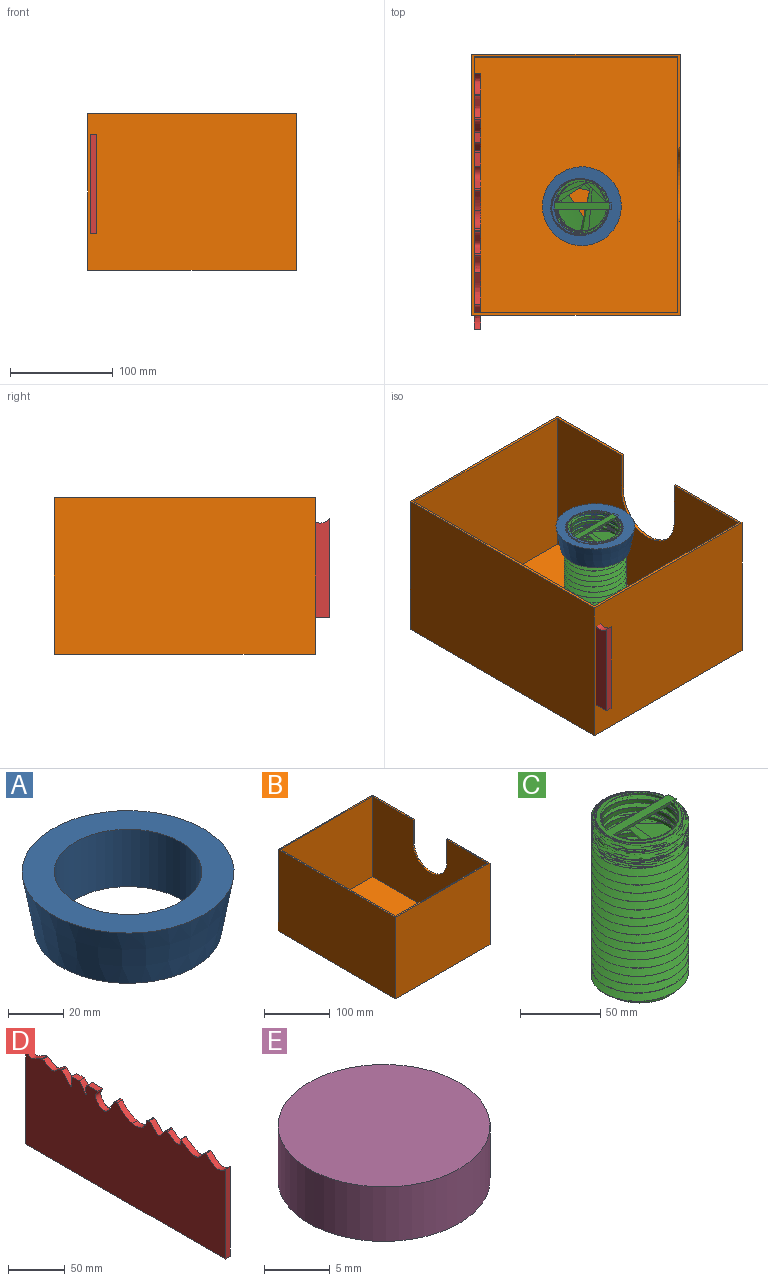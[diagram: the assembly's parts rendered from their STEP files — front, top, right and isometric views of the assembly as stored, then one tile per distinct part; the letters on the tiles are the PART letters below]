
ASSEMBLY  parts=5 mates=4
PART A: 4 faces, bbox 76.7x76.7x25.4 mm
  f0: cone r=38.36mm half-angle=10deg, axis (0,0,1), area 5854.3mm2, adj f1,f2
  f1: plane 67.77x67.77mm, normal (0,0,-1), area 1371mm2, adj f0,f3
  f2: plane 76.73x76.73mm, normal (0,0,1), area 2387.6mm2, adj f0,f3
  f3: cylinder r=26.68mm len=53.36mm, axis (0,0,1), area 4258.1mm2, adj f1,f2
PART B: 14 faces, bbox 203.2x254x152.4 mm
  f0: plane 254x203.2mm, normal (0,0,1), area 2113.4mm2, adj f1,f2,f3,f4,f6,f7,f8,f9
  f1: plane 254x152.4mm, normal (1,0,0), area 33505.9mm2, adj f0,f2,f3,f5,f11,f12,f13
  f2: plane 203.2x152.4mm, normal (0,-1,0), area 30967.7mm2, adj f0,f1,f4,f5
  f3: plane 203.2x152.4mm, normal (0,1,0), area 30967.7mm2, adj f0,f1,f4,f5
  f4: plane 254x152.4mm, normal (-1,0,0), area 38709.6mm2, adj f0,f2,f3,f5
  f5: plane 254x203.2mm, normal (0,0,-1), area 51612.8mm2, adj f1,f2,f3,f4
  f6: plane 198.12x149.86mm, normal (0,1,0), area 29690.3mm2, adj f0,f7,f9,f10
  f7: plane 248.92x149.86mm, normal (-1,0,0), area 32099.4mm2, adj f0,f6,f8,f10,f11,f12,f13
  f8: plane 198.12x149.86mm, normal (0,-1,0), area 29690.3mm2, adj f0,f7,f9,f10
  f9: plane 248.92x149.86mm, normal (1,0,0), area 37303.2mm2, adj f0,f6,f8,f10
  f10: plane 248.92x198.12mm, normal (0,0,1), area 49316mm2, adj f6,f7,f8,f9
  f11: cylinder r=36.1mm len=72.19mm, axis (1,0,0), area 288mm2, adj f1,f7,f12,f13
  f12: plane 43.73x2.54mm, normal (0,-1,0), area 111.1mm2, adj f0,f1,f7,f11
  f13: plane 43.73x2.54mm, normal (0,1,0), area 111.1mm2, adj f0,f1,f7,f11
PART C: 24 faces, bbox 61x70.4x130.7 mm
  f0: bspline ~129.9x70.39mm, area 19670.9mm2, adj f2,f4,f7,f8,f9,f10,f12,f13
  f1: plane 50.8x50.8mm, normal (0,0,-1), area 144.9mm2, adj f2,f8,f10,f17,f21,f23
  f2: cylinder r=25.4mm len=3.62mm, axis (0,0,-1), area 0.3mm2, adj f0,f1,f23
  f3: cylinder r=25.4mm len=21.06mm, axis (0,0,-1), area 16.7mm2, adj f4,f5,f16
  f4: bspline ~127.79x70.39mm, area 19401.9mm2, adj f0,f3,f5,f7,f8,f9,f11,f16
  f5: plane 3.38x1.91mm, normal (0,1,0), area 5.9mm2, adj f3,f4,f6,f11,f16
  f6: plane 6.35x1.91mm, normal (1,0,0), area 12.1mm2, adj f5,f7,f11,f16
  f7: plane 3.38x1.91mm, normal (0,-1,0), area 6.1mm2, adj f0,f4,f6,f8,f11,f16
  f8: cylinder r=25.4mm len=125.29mm, axis (0,0,-1), area 4509mm2, adj f0,f1,f4,f7,f9
  f9: plane 5.08x5.08mm, normal (0,-1,0), area 12.9mm2, adj f0,f4,f8,f10
  f10: cylinder r=25.4mm len=1.59mm, axis (0,0,-1), area 2mm2, adj f0,f1,f9,f17
  f11: plane 6.39x2.36mm, normal (0,0,-1), area 12.5mm2, adj f4,f5,f6,f7
  f12: plane 6.35x0.51mm, normal (-1,0,0), area 2.2mm2, adj f0,f13,f14,f15
  f13: plane 0.6x0.3mm, normal (0,1,0), area 0.1mm2, adj f0,f12,f15
  f14: plane 1.04x0.51mm, normal (0,-1,0), area 0.3mm2, adj f0,f12,f15
  f15: plane 6.39x1.07mm, normal (0,0,-1), area 4.4mm2, adj f0,f12,f13,f14
  f16: plane 57.85x54.78mm, normal (0,0,1), area 729.5mm2, adj f0,f3,f4,f5,f6,f7,f19,f20
  f17: plane 4.3x3.51mm, normal (0,1,0), area 7.4mm2, adj f0,f1,f10,f21,f22
  f18: plane 49.3x6.35mm, normal (0,0,-1), area 311.7mm2, adj f19,f20,f21
  f19: plane 51.38x1.91mm, normal (0,-1,0), area 95.7mm2, adj f16,f18,f21
  f20: plane 51.38x1.91mm, normal (0,1,0), area 96mm2, adj f16,f18,f21
  f21: cylinder r=24.13mm len=125.41mm, axis (0,0,-1), area 10865.2mm2, adj f1,f16,f17,f18,f19,f20,f23
  f22: cylinder r=26.67mm len=17.56mm, axis (0,0,1), area 27.9mm2, adj f0,f17,f23
  f23: extruded ~29.92x6.35mm, area 43.4mm2, adj f0,f1,f2,f21,f22
PART D: 26 faces, bbox 6.4x249.9x102.7 mm
  f0: plane 6.35x0.45mm, normal (0,0,1), area 2.8mm2, adj f8,f9,f16,f24
  f1: plane 6.35x0.21mm, normal (0,0,1), area 1.4mm2, adj f8,f9,f23,f24
  f2: plane 6.35x1.63mm, normal (0,0,1), area 10.4mm2, adj f8,f9,f22,f23
  f3: plane 6.35x2mm, normal (0,0,1), area 12.7mm2, adj f8,f9,f14,f21
  f4: plane 13.33x6.35mm, normal (0,0,1), area 84.7mm2, adj f8,f9,f20,f21
  f5: plane 9.24x6.35mm, normal (0,0,1), area 58.7mm2, adj f8,f9,f19,f20
  f6: plane 6.35x1.71mm, normal (0,0,1), area 10.8mm2, adj f8,f9,f18,f19
  f7: plane 6.35x0.95mm, normal (0,0,1), area 6mm2, adj f8,f9,f15,f22
  f8: plane 249.92x102.66mm, normal (1,0,0), area 23908mm2, adj f0,f1,f2,f3,f4,f5,f6,f7
  f9: plane 249.92x102.66mm, normal (-1,0,0), area 23908mm2, adj f0,f1,f2,f3,f4,f5,f6,f7
  f10: plane 248.92x6.35mm, normal (0,0,-1), area 1580.6mm2, adj f8,f9,f11,f13
  f11: plane 101.6x6.35mm, normal (0,1,0), area 645.2mm2, adj f8,f9,f10,f17
  f12: plane 6.35x0.73mm, normal (0,0,1), area 4.6mm2, adj f8,f9,f17,f18
  f13: plane 97.03x6.35mm, normal (0,-1,0), area 616.1mm2, adj f8,f9,f10,f16
  f14: extruded ~19.35x12.8mm, area 150mm2, adj f3,f8,f9,f25
  f15: extruded ~6.35x2.3mm, area 20.7mm2, adj f7,f8,f9,f25
  f16: extruded ~24.06x9.26mm, area 182.4mm2, adj f0,f8,f9,f13
  f17: extruded ~19.97x6.35mm, area 149.1mm2, adj f8,f9,f11,f12
  f18: extruded ~22.19x6.35mm, area 160.1mm2, adj f6,f8,f9,f12
  f19: extruded ~12.73x11.6mm, area 181.1mm2, adj f5,f6,f8,f9
  f20: extruded ~10.56x9.91mm, area 156.9mm2, adj f4,f5,f8,f9
  f21: extruded ~24.61x16.98mm, area 291.5mm2, adj f3,f4,f8,f9
  f22: extruded ~21.31x9.63mm, area 187mm2, adj f2,f7,f8,f9
  f23: extruded ~16.74x6.88mm, area 153.9mm2, adj f1,f2,f8,f9
  f24: extruded ~30.84x9.53mm, area 235.7mm2, adj f0,f1,f8,f9
  f25: cylinder r=12.85mm len=17.33mm, axis (1,0,0), area 148.7mm2, adj f8,f9,f14,f15
PART E: 3 faces, bbox 16.2x16.2x5.1 mm
  f0: cylinder r=8.08mm len=16.16mm, axis (0,0,-1), area 257.9mm2, adj f1,f2
  f1: plane 16.16x16.16mm, normal (0,0,1), area 205.1mm2, adj f0
  f2: plane 16.16x16.16mm, normal (0,0,-1), area 205.1mm2, adj f0
PLACE A t=(-89.27,-16.97,25.54)mm
PLACE B t=(-94.99,3.97,7.89)mm
PLACE C t=(-89.27,-16.97,25.54)mm
PLACE D t=(-94.99,-12.57,23.09)mm
PLACE E rot(axis=(1,0,0),90deg) t=(-124.71,-15.7,-23.1)mm
MATE slider D.f4 <-> C.f16  axis (0,0,1) through (-190.87,28.75,144.86)mm
MATE fastened A.f3 <-> C.f2  axis (0,0,1) through (-89.27,-16.97,150.96)mm
MATE planar B.f9 <-> D.f9  axis (1,0,0) through (-194.05,3.97,85.36)mm
MATE fastened E.f0 <-> C.f17  axis (0,1,0) through (-63.77,-15.7,26.27)mm
